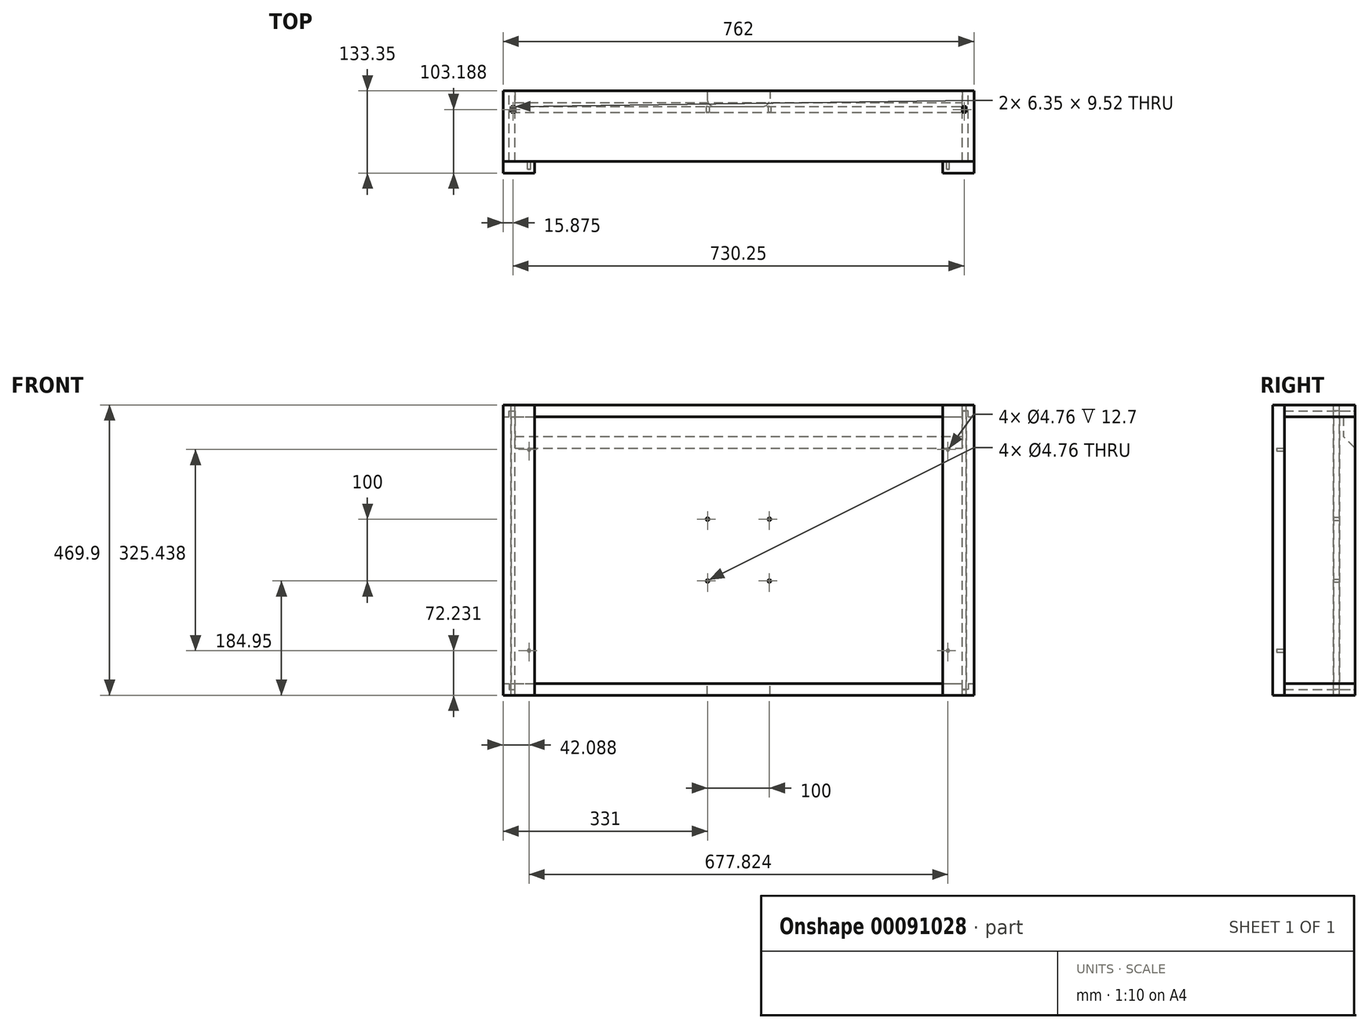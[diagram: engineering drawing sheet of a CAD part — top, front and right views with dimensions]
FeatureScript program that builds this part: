
annotation { "Feature Type Name" : "Feature", "Feature Type Description" : "" }
export const myFeature = defineFeature(function(context is Context, id is Id, definition is map)
    precondition{}
    {
        {
            var Q0;
            Q0=qCreatedBy(makeId("Front.planeOp"),FACE);
            var sketch = newSketch(context, id + "F0", { "sketchPlane" : qUnion([Q0])});
            skLineSegment(sketch, "E0.bottom", {"start": v(381, 234.95) * mm, "end": v(-381, 234.95) * mm, "construction": true});
            skLineSegment(sketch, "E0.top", {"start": v(381, -234.95) * mm, "end": v(-381, -234.95) * mm, "construction": true});
            skLineSegment(sketch, "E0.left", {"start": v(381, 234.95) * mm, "end": v(381, -234.95) * mm, "construction": true});
            skLineSegment(sketch, "E0.right", {"start": v(-381, 234.95) * mm, "end": v(-381, -234.95) * mm, "construction": true});
            skPoint(sketch, "E0.middle", {"position": v(0, 0) * mm});
            skSolve(sketch);
        }
        {
            var Q0;
            Q0=qCreatedBy(makeId("Front.planeOp"),FACE);
            var sketch = newSketch(context, id + "F1", { "sketchPlane" : qUnion([Q0])});
            skLineSegment(sketch, "E1.bottom", {"start": v(-381, 234.95) * mm, "end": v(381, 234.95) * mm});
            skLineSegment(sketch, "E1.top", {"start": v(-381, 215.9) * mm, "end": v(-371.48, 215.9) * mm});
            skLineSegment(sketch, "E1.left", {"start": v(-381, 234.95) * mm, "end": v(-381, 215.9) * mm});
            skLineSegment(sketch, "E1.right", {"start": v(381, 234.95) * mm, "end": v(381, 215.9) * mm});
            skLineSegment(sketch, "E2", {"start": v(-371.48, 215.9) * mm, "end": v(-371.48, 225.42) * mm});
            skLineSegment(sketch, "E3", {"start": v(-371.48, 225.42) * mm, "end": v(-361.95, 225.42) * mm});
            skLineSegment(sketch, "E4", {"start": v(-361.95, 225.42) * mm, "end": v(-361.95, 215.9) * mm});
            skLineSegment(sketch, "E5", {"start": v(371.48, 215.9) * mm, "end": v(371.48, 225.43) * mm});
            skLineSegment(sketch, "E6", {"start": v(371.48, 225.43) * mm, "end": v(361.95, 225.43) * mm});
            skLineSegment(sketch, "E7", {"start": v(361.95, 225.43) * mm, "end": v(361.95, 215.9) * mm});
            skLineSegment(sketch, "E8.trimOffspring", {"start": v(-361.95, 215.9) * mm, "end": v(361.95, 215.9) * mm});
            skLineSegment(sketch, "E9.trimOffspring", {"start": v(371.48, 215.9) * mm, "end": v(381, 215.9) * mm});
            skSolve(sketch);
        }
        {
            var Q0;
            Q0=qCreatedBy(makeId("Front.planeOp"),FACE);
            var sketch = newSketch(context, id + "F2", { "sketchPlane" : qUnion([Q0])});
            skLineSegment(sketch, "E10.bottom", {"start": v(-381, -234.95) * mm, "end": v(381, -234.95) * mm});
            skLineSegment(sketch, "E10.top", {"start": v(-381, -215.9) * mm, "end": v(-371.48, -215.9) * mm});
            skLineSegment(sketch, "E10.left", {"start": v(-381, -234.95) * mm, "end": v(-381, -215.9) * mm});
            skLineSegment(sketch, "E10.right", {"start": v(381, -234.95) * mm, "end": v(381, -215.9) * mm});
            skLineSegment(sketch, "E11", {"start": v(371.48, -215.9) * mm, "end": v(371.48, -225.43) * mm});
            skLineSegment(sketch, "E12", {"start": v(371.48, -225.43) * mm, "end": v(361.95, -225.43) * mm});
            skLineSegment(sketch, "E13", {"start": v(361.95, -225.43) * mm, "end": v(361.95, -215.9) * mm});
            skLineSegment(sketch, "E14", {"start": v(-371.48, -215.9) * mm, "end": v(-371.48, -225.43) * mm});
            skLineSegment(sketch, "E15", {"start": v(-371.48, -225.43) * mm, "end": v(-361.95, -225.43) * mm});
            skLineSegment(sketch, "E16", {"start": v(-361.95, -225.43) * mm, "end": v(-361.95, -215.9) * mm});
            skLineSegment(sketch, "E17.trimOffspring", {"start": v(-361.95, -215.9) * mm, "end": v(361.95, -215.9) * mm});
            skLineSegment(sketch, "E18.trimOffspring", {"start": v(371.48, -215.9) * mm, "end": v(381, -215.9) * mm});
            skSolve(sketch);
        }
        {
            var Q0;
            Q0=qCreatedBy(makeId("Front.planeOp"),FACE);
            var sketch = newSketch(context, id + "F3", { "sketchPlane" : qUnion([Q0])});
            skLineSegment(sketch, "E19.bottom", {"start": v(-381, 215.9) * mm, "end": v(-371.48, 215.9) * mm});
            skLineSegment(sketch, "E19.top", {"start": v(-381, -215.9) * mm, "end": v(-371.48, -215.9) * mm});
            skLineSegment(sketch, "E19.left", {"start": v(-381, 215.9) * mm, "end": v(-381, -215.9) * mm});
            skLineSegment(sketch, "E19.right", {"start": v(-361.95, 215.9) * mm, "end": v(-361.95, -215.9) * mm});
            skLineSegment(sketch, "E20.bottom", {"start": v(371.48, 215.9) * mm, "end": v(381, 215.9) * mm});
            skLineSegment(sketch, "E20.top", {"start": v(371.48, -215.9) * mm, "end": v(381, -215.9) * mm});
            skLineSegment(sketch, "E20.left", {"start": v(361.95, 215.9) * mm, "end": v(361.95, -215.9) * mm});
            skLineSegment(sketch, "E20.right", {"start": v(381, 215.9) * mm, "end": v(381, -215.9) * mm});
            skLineSegment(sketch, "E21", {"start": v(-361.95, 215.9) * mm, "end": v(-361.95, 225.42) * mm});
            skLineSegment(sketch, "E22", {"start": v(-361.95, 225.43) * mm, "end": v(-371.48, 225.43) * mm});
            skLineSegment(sketch, "E23", {"start": v(-371.48, 225.42) * mm, "end": v(-371.48, 215.9) * mm});
            skLineSegment(sketch, "E24", {"start": v(-361.95, -215.9) * mm, "end": v(-361.95, -225.43) * mm});
            skLineSegment(sketch, "E25", {"start": v(-361.95, -225.43) * mm, "end": v(-371.48, -225.43) * mm});
            skLineSegment(sketch, "E26", {"start": v(-371.48, -225.43) * mm, "end": v(-371.48, -215.9) * mm});
            skLineSegment(sketch, "E27", {"start": v(361.95, 215.9) * mm, "end": v(361.95, 225.43) * mm});
            skLineSegment(sketch, "E28", {"start": v(361.95, 225.43) * mm, "end": v(371.48, 225.43) * mm});
            skLineSegment(sketch, "E29", {"start": v(371.48, 225.43) * mm, "end": v(371.48, 215.9) * mm});
            skLineSegment(sketch, "E30", {"start": v(361.95, -215.9) * mm, "end": v(361.95, -225.43) * mm});
            skLineSegment(sketch, "E31", {"start": v(361.95, -225.43) * mm, "end": v(371.48, -225.43) * mm});
            skLineSegment(sketch, "E32", {"start": v(371.48, -225.43) * mm, "end": v(371.48, -215.9) * mm});
            skSolve(sketch);
        }
        {
            var Q0;
            Q0=makeQuery(id+"F1.imprint","IMPRINT",FACE,{"disambiguationData":[TD([[makeQuery(id+"F1.imprint","IMPRINT",EDGE,{"derivedFrom":sQuery(id+"F1.wireOp",EDGE,"E1.bottom")}),-1.0]])]});
            var Q1;
            Q1=makeQuery(id+"F3.imprint","IMPRINT",FACE,{"disambiguationData":[TD([[makeQuery(id+"F3.imprint","IMPRINT",EDGE,{"derivedFrom":sQuery(id+"F3.wireOp",EDGE,"E19.bottom")}),-1.0]])]});
            var Q2;
            Q2=makeQuery(id+"F3.imprint","IMPRINT",FACE,{"disambiguationData":[TD([[makeQuery(id+"F3.imprint","IMPRINT",EDGE,{"derivedFrom":sQuery(id+"F3.wireOp",EDGE,"E20.bottom")}),-1.0]])]});
            var Q3;
            Q3=makeQuery(id+"F2.imprint","IMPRINT",FACE,{"disambiguationData":[TD([[makeQuery(id+"F2.imprint","IMPRINT",EDGE,{"derivedFrom":sQuery(id+"F2.wireOp",EDGE,"E10.bottom")}),1.0]])]});
            extrude(context, id + "F4", {"entities" : qUnion([Q0, Q1, Q2, Q3]), "depth" : 114.3 * mm});
        }
        {
            var Q0;
            Q0=qCreatedBy(makeId("Top.planeOp"),FACE);
            var sketch = newSketch(context, id + "F5", { "sketchPlane" : qUnion([Q0])});
            skLineSegment(sketch, "E33.bottom", {"start": v(-368.3, -25.4) * mm, "end": v(-361.95, -25.4) * mm});
            skLineSegment(sketch, "E33.top", {"start": v(-368.3, -34.93) * mm, "end": v(-361.95, -34.92) * mm});
            skLineSegment(sketch, "E33.left", {"start": v(-361.95, -25.4) * mm, "end": v(-361.95, -34.92) * mm});
            skLineSegment(sketch, "E33.right", {"start": v(-368.3, -25.4) * mm, "end": v(-368.3, -34.93) * mm});
            skLineSegment(sketch, "E34.MirrorCS", {"start": v(368.3, -25.4) * mm, "end": v(361.95, -25.4) * mm});
            skLineSegment(sketch, "E35.MirrorCS", {"start": v(368.3, -34.92) * mm, "end": v(361.95, -34.92) * mm});
            skLineSegment(sketch, "E36.MirrorCS", {"start": v(361.95, -25.4) * mm, "end": v(361.95, -34.92) * mm});
            skLineSegment(sketch, "E37.MirrorCS", {"start": v(368.3, -25.4) * mm, "end": v(368.3, -34.93) * mm});
            skSolve(sketch);
        }
        {
            var Q0;
            Q0=makeQuery(id+"F5.imprint","IMPRINT",FACE,{"disambiguationData":[TD([[makeQuery(id+"F5.imprint","IMPRINT",EDGE,{"derivedFrom":sQuery(id+"F5.wireOp",EDGE,"E33.bottom")}),-1.0]])]});
            var Q1;
            Q1=makeQuery(id+"F5.imprint","IMPRINT",FACE,{"disambiguationData":[TD([[makeQuery(id+"F5.imprint","IMPRINT",EDGE,{"derivedFrom":sQuery(id+"F5.wireOp",EDGE,"E34.MirrorCS")}),1.0]])]});
            extrude(context, id + "F6", {"entities" : qUnion([Q0, Q1]), "operationType" : NewBodyOperationType.REMOVE, "endBound" : BoundingType.THROUGH_ALL, "oppositeDirection" : true, "depth" : 25.4 * mm, "hasSecondDirection" : true, "secondDirectionBound" : SecondDirectionBoundingType.THROUGH_ALL, "secondDirectionOppositeDirection" : false, "secondDirectionDepth" : 25.4 * mm});
        }
        {
            var Q0;
            Q0=makeQuery(id+"F4.opExtrude","CAP_FACE",FACE,{"disambiguationData":[OSD([sQuery(id+"F1.wireOp",EDGE,"E1.bottom"),sQuery(id+"F1.wireOp",EDGE,"E1.top"),sQuery(id+"F1.wireOp",EDGE,"E1.left"),sQuery(id+"F1.wireOp",EDGE,"E1.right"),sQuery(id+"F1.wireOp",EDGE,"E2"),sQuery(id+"F1.wireOp",EDGE,"E3"),sQuery(id+"F1.wireOp",EDGE,"E4"),sQuery(id+"F1.wireOp",EDGE,"E5"),sQuery(id+"F1.wireOp",EDGE,"E6"),sQuery(id+"F1.wireOp",EDGE,"E7"),sQuery(id+"F1.wireOp",EDGE,"E8.trimOffspring"),sQuery(id+"F1.wireOp",EDGE,"E9.trimOffspring")])],"isStart":false});
            var sketch = newSketch(context, id + "F7", { "sketchPlane" : qUnion([Q0])});
            skLineSegment(sketch, "E38.bottom", {"start": v(-381, 234.95) * mm, "end": v(-330.2, 234.95) * mm});
            skLineSegment(sketch, "E38.top", {"start": v(-381, -234.95) * mm, "end": v(-330.2, -234.95) * mm});
            skLineSegment(sketch, "E38.left", {"start": v(-381, 234.95) * mm, "end": v(-381, -234.95) * mm});
            skLineSegment(sketch, "E38.right", {"start": v(-330.2, 234.95) * mm, "end": v(-330.2, -234.95) * mm});
            skLineSegment(sketch, "E39.bottom", {"start": v(381, 234.95) * mm, "end": v(330.2, 234.95) * mm});
            skLineSegment(sketch, "E39.top", {"start": v(381, -234.95) * mm, "end": v(330.2, -234.95) * mm});
            skLineSegment(sketch, "E39.left", {"start": v(381, 234.95) * mm, "end": v(381, -234.95) * mm});
            skLineSegment(sketch, "E39.right", {"start": v(330.2, 234.95) * mm, "end": v(330.2, -234.95) * mm});
            skSolve(sketch);
        }
        {
            var Q0;
            {var subQ1=sQuery(id+"F7.wireOp",EDGE,"E39.top");Q0=makeQuery(id+"F7.imprint","IMPRINT",FACE,{"disambiguationData":[TD([[makeQuery(id+"F7.imprint","IMPRINT",EDGE,{"derivedFrom":subQ1}),-1.0]])]});}
            var Q1;
            {var subQ1=sQuery(id+"F7.wireOp",EDGE,"E39.bottom");Q1=makeQuery(id+"F7.imprint","IMPRINT",FACE,{"disambiguationData":[TD([[makeQuery(id+"F7.imprint","IMPRINT",EDGE,{"derivedFrom":subQ1}),-1.0]])]});}
            extrude(context, id + "F8", {"entities" : qUnion([Q0, Q1]), "depth" : 19.05 * mm});
        }
        {
            var Q0;
            Q0=makeQuery(id+"F4.opExtrude","SWEPT_FACE",FACE,{"disambiguationData":[OSD([sQuery(id+"F2.wireOp",EDGE,"E17.trimOffspring")])]});
            var sketch = newSketch(context, id + "F9", { "sketchPlane" : qUnion([Q0])});
            skLineSegment(sketch, "E40.bottom", {"start": v(-50.8, 0) * mm, "end": v(50.8, 0) * mm});
            skLineSegment(sketch, "E40.top", {"start": v(-38.1, -25.4) * mm, "end": v(38.1, -25.4) * mm});
            skLineSegment(sketch, "E40.left", {"start": v(-50.8, 0) * mm, "end": v(-50.8, -12.7) * mm});
            skLineSegment(sketch, "E40.right", {"start": v(50.8, 0) * mm, "end": v(50.8, -12.7) * mm});
            skLineSegment(sketch, "E41", {"start": v(0, 0) * mm, "end": v(0, -66.2) * mm, "construction": true});
            skPoint(sketch, "E41.endSnap0", {"position": v(0, 0) * mm});
            skPoint(sketch, "E42.visualSharp", {"position": v(-50.8, -25.4) * mm});
            skArc(sketch, "E42.filletArc", {"start": v(-50.8, -12.7) * mm, "mid": v(-47.08, -21.68) * mm, "end": v(-38.1, -25.4) * mm});
            skPoint(sketch, "E43.visualSharp", {"position": v(50.8, -25.4) * mm});
            skArc(sketch, "E43.filletArc", {"start": v(38.1, -25.4) * mm, "mid": v(47.08, -21.68) * mm, "end": v(50.8, -12.7) * mm});
            skSolve(sketch);
        }
        {
            var Q0;
            Q0=makeQuery(id+"F9.imprint","IMPRINT",FACE,{"disambiguationData":[TD([[makeQuery(id+"F9.imprint","IMPRINT",EDGE,{"derivedFrom":sQuery(id+"F9.wireOp",EDGE,"E40.bottom")}),-1.0]])]});
            extrude(context, id + "F10", {"entities" : qUnion([Q0]), "operationType" : NewBodyOperationType.REMOVE, "oppositeDirection" : true, "depth" : 25.4 * mm});
        }
        {
            var Q0;
            Q0=makeQuery(id+"F4.opExtrude","SWEPT_FACE",FACE,{"disambiguationData":[OSD([sQuery(id+"F3.wireOp",EDGE,"E20.left"),sQuery(id+"F3.wireOp",EDGE,"E27"),sQuery(id+"F3.wireOp",EDGE,"E30")])]});
            var sketch = newSketch(context, id + "F11", { "sketchPlane" : qUnion([Q0])});
            skLineSegment(sketch, "E44.bottom", {"start": v(0, 215.9) * mm, "end": v(19.05, 215.9) * mm});
            skLineSegment(sketch, "E44.left", {"start": v(0, 215.9) * mm, "end": v(0, 165.1) * mm});
            skLineSegment(sketch, "E44.right", {"start": v(19.05, 215.9) * mm, "end": v(19.05, 184.15) * mm});
            skLineSegment(sketch, "E45", {"start": v(0, 165.1) * mm, "end": v(19.05, 184.15) * mm});
            skSolve(sketch);
        }
        {
            var Q0;
            Q0=makeQuery(id+"F11.imprint","IMPRINT",FACE,{"disambiguationData":[TD([[makeQuery(id+"F11.imprint","IMPRINT",EDGE,{"derivedFrom":sQuery(id+"F11.wireOp",EDGE,"E44.bottom")}),-1.0]])]});
            extrude(context, id + "F12", {"entities" : qUnion([Q0]), "endBound" : BoundingType.UP_TO_NEXT, "depth" : 25.4 * mm});
        }
        {
            var Q0;
            Q0=makeQuery(id+"F8.opExtrude","CAP_FACE",FACE,{"disambiguationData":[OSD([sQuery(id+"F7.wireOp",EDGE,"E39.bottom"),sQuery(id+"F7.wireOp",EDGE,"E39.top"),sQuery(id+"F7.wireOp",EDGE,"E39.left"),sQuery(id+"F7.wireOp",EDGE,"E39.right")])],"isStart":true});
            var sketch = newSketch(context, id + "F13", { "sketchPlane" : qUnion([Q0])});
            skCircle(sketch, "E46", {"center": v(-338.91, 162.72) * mm, "radius": 2.38 * mm});
            skCircle(sketch, "E47", {"center": v(-338.91, -162.72) * mm, "radius": 2.38 * mm});
            skLineSegment(sketch, "E48", {"start": v(-338.91, 162.72) * mm, "end": v(-338.91, -162.72) * mm, "construction": true});
            skSolve(sketch);
        }
        {
            var Q0;
            Q0 = qSketchRegion(id + "F13", true);
            extrude(context, id + "F14", {"entities" : qUnion([Q0]), "operationType" : NewBodyOperationType.REMOVE, "oppositeDirection" : true, "depth" : 12.7 * mm});
        }
        {
            var Q0;
            Q0=qCreatedBy(makeId("Top.planeOp"),FACE);
            var sketch = newSketch(context, id + "F15", { "sketchPlane" : qUnion([Q0])});
            skLineSegment(sketch, "E49.bottom", {"start": v(-368.3, -25.4) * mm, "end": v(368.3, -25.4) * mm});
            skLineSegment(sketch, "E49.top", {"start": v(-368.3, -34.93) * mm, "end": v(368.3, -34.93) * mm});
            skLineSegment(sketch, "E49.left", {"start": v(-368.3, -25.4) * mm, "end": v(-368.3, -34.93) * mm});
            skLineSegment(sketch, "E49.right", {"start": v(368.3, -25.4) * mm, "end": v(368.3, -34.93) * mm});
            skSolve(sketch);
        }
        {
            var Q0;
            Q0=makeQuery(id+"F15.imprint","IMPRINT",FACE,{"disambiguationData":[TD([[makeQuery(id+"F15.imprint","IMPRINT",EDGE,{"derivedFrom":sQuery(id+"F15.wireOp",EDGE,"E49.bottom")}),-1.0]])]});
            var Q1;
            Q1=makeQuery(id+"F4.opExtrude","SWEPT_FACE",FACE,{"disambiguationData":[OSD([sQuery(id+"F1.wireOp",EDGE,"E8.trimOffspring")])]});
            var Q2;
            Q2=makeQuery(id+"F4.opExtrude","SWEPT_FACE",FACE,{"disambiguationData":[OSD([sQuery(id+"F2.wireOp",EDGE,"E17.trimOffspring")])]});
            extrude(context, id + "F16", {"entities" : qUnion([Q0]), "endBound" : BoundingType.UP_TO_SURFACE, "endBoundEntityFace" : qUnion([Q1]), "depth" : 25.4 * mm, "hasSecondDirection" : true, "secondDirectionBound" : SecondDirectionBoundingType.UP_TO_SURFACE, "secondDirectionOppositeDirection" : true, "secondDirectionBoundEntityFace" : qUnion([Q2]), "secondDirectionDepth" : 25.4 * mm});
        }
        {
            var Q0;
            Q0=makeQuery(id+"F8.opExtrude","SWEPT_BODY",BODY,{"disambiguationData":[OSD([sQuery(id+"F7.wireOp",EDGE,"E39.bottom"),sQuery(id+"F7.wireOp",EDGE,"E39.top"),sQuery(id+"F7.wireOp",EDGE,"E39.left"),sQuery(id+"F7.wireOp",EDGE,"E39.right")])]});
            var Q1;
            Q1=qCreatedBy(makeId("Right.planeOp"),FACE);
            mirror(context, id + "F17", {"entities" : qUnion([Q0]), "mirrorPlane" : qUnion([Q1])});
        }
        {
            var Q0;
            Q0=makeQuery(id+"F16.opExtrude","SWEPT_FACE",FACE,{"disambiguationData":[OSD([sQuery(id+"F15.wireOp",EDGE,"E49.top")])]});
            var sketch = newSketch(context, id + "F18", { "sketchPlane" : qUnion([Q0])});
            skCircle(sketch, "E50", {"center": v(-50, 50) * mm, "radius": 2.38 * mm});
            skCircle(sketch, "E51", {"center": v(50, 50) * mm, "radius": 2.38 * mm});
            skCircle(sketch, "E52", {"center": v(-50, -50) * mm, "radius": 2.38 * mm});
            skCircle(sketch, "E53", {"center": v(50, -50) * mm, "radius": 2.38 * mm});
            skLineSegment(sketch, "E54.bottom", {"start": v(-50, 50) * mm, "end": v(50, 50) * mm, "construction": true});
            skLineSegment(sketch, "E54.top", {"start": v(-50, -50) * mm, "end": v(50, -50) * mm, "construction": true});
            skLineSegment(sketch, "E54.left", {"start": v(-50, 50) * mm, "end": v(-50, -50) * mm, "construction": true});
            skLineSegment(sketch, "E54.right", {"start": v(50, 50) * mm, "end": v(50, -50) * mm, "construction": true});
            skLineSegment(sketch, "E55", {"start": v(0, 215.9) * mm, "end": v(0, -215.9) * mm});
            skLineSegment(sketch, "E56", {"start": v(-50, 50) * mm, "end": v(50, -50) * mm, "construction": true});
            skSolve(sketch);
        }
        {
            var Q0;
            Q0=makeQuery(id+"F18.imprint","IMPRINT",FACE,{"disambiguationData":[TD([[makeQuery(id+"F18.imprint","IMPRINT",EDGE,{"derivedFrom":sQuery(id+"F18.wireOp",EDGE,"E50")}),1.0]])]});
            var Q1;
            Q1=makeQuery(id+"F18.imprint","IMPRINT",FACE,{"disambiguationData":[TD([[makeQuery(id+"F18.imprint","IMPRINT",EDGE,{"derivedFrom":sQuery(id+"F18.wireOp",EDGE,"E51")}),1.0]])]});
            var Q2;
            Q2=makeQuery(id+"F18.imprint","IMPRINT",FACE,{"disambiguationData":[TD([[makeQuery(id+"F18.imprint","IMPRINT",EDGE,{"derivedFrom":sQuery(id+"F18.wireOp",EDGE,"E52")}),1.0]])]});
            var Q3;
            Q3=makeQuery(id+"F18.imprint","IMPRINT",FACE,{"disambiguationData":[TD([[makeQuery(id+"F18.imprint","IMPRINT",EDGE,{"derivedFrom":sQuery(id+"F18.wireOp",EDGE,"E53")}),1.0]])]});
            extrude(context, id + "F19", {"entities" : qUnion([Q0, Q1, Q2, Q3]), "operationType" : NewBodyOperationType.REMOVE, "endBound" : BoundingType.THROUGH_ALL, "oppositeDirection" : true, "depth" : 25.4 * mm});
        }
    });
